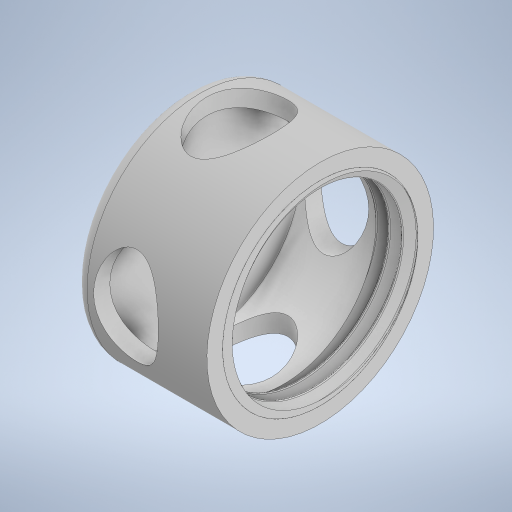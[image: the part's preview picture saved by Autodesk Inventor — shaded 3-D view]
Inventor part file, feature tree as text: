
AUTODESK INVENTOR PART (.ipt)
format: ipt  version: 2023 (Build 270158000, 158)  size: 604,672 bytes
history: native  units: in
note: dims shown in document units (in); Inventor stores cm internally (conversion verified against a paired STEP export)
features: sketch x6, extrude x5, fillet x1, thread x1, revolve x1, helix x1
ambient origin geometry x8: Origin, YZ Plane, XZ Plane, XY Plane, X Axis, Y Axis, Z Axis, Center Point
bodies: Solid1 (feature_tree), Solid7 (feature_tree)
feature tree (15):
  sketch  "Sketch1"  dims[d0=1.1811in d1=1.378in]
  extrude  "Extrusion2"  Depth=1.378in
  sketch  "Sketch2"  dims[d4=0.0984in d5=0.0in d6=0.1969in]
  sketch  "Sketch3"  dims[d7=0.2953in d8=0.315in]
  extrude  "Extrusion3"  Depth=0.1969in
  extrude  "Extrusion4"  Depth=0.315in
  extrude  "Extrusion5"  Depth=0.2953in
  fillet  "Fillet1"  Radius=0.315in
  extrude  "Extrusion7"  Depth=0.8071in TaperAngle=0.0deg
  thread  "Thread6"  [1 undecoded]
  revolve  "Revolution6"  [1 undecoded]
  helix  "Coil6"  [1 undecoded]
  sketch  "Sketch8"  dims[d9=0.1969in d10=0.2953in d11=0.315in]
  sketch  "Sketch15"  dims[d12=0.8071in d13=0.0in d14=1.5748in d15=0.0in d16=1.5748in d17=0.0in]
  sketch  "Sketch16"  dims[d27=0.3779in d38=0.0787in d48=0.3779in d59=1.187in d71=0.3779in d92=0.3779in d103=0.1969in d104=0.0in d114=0.3779in d125=0.1969in d126=0.0in d127=0.3779in d128=0.0126in d129=0.0126in d132=0.0787in d134=0.3779in d136=0.0in d137=0.0788in d138=0.3543in d139=0.3937in d140=0.0in d141=0.0in d142=0.0in d143=0.0in d144=0.0in]
note: 3 required parameter values undecoded (feature->parameter linkage not recoverable at this tier; creation-order binding heuristic only, values carry confidence <= 0.55)